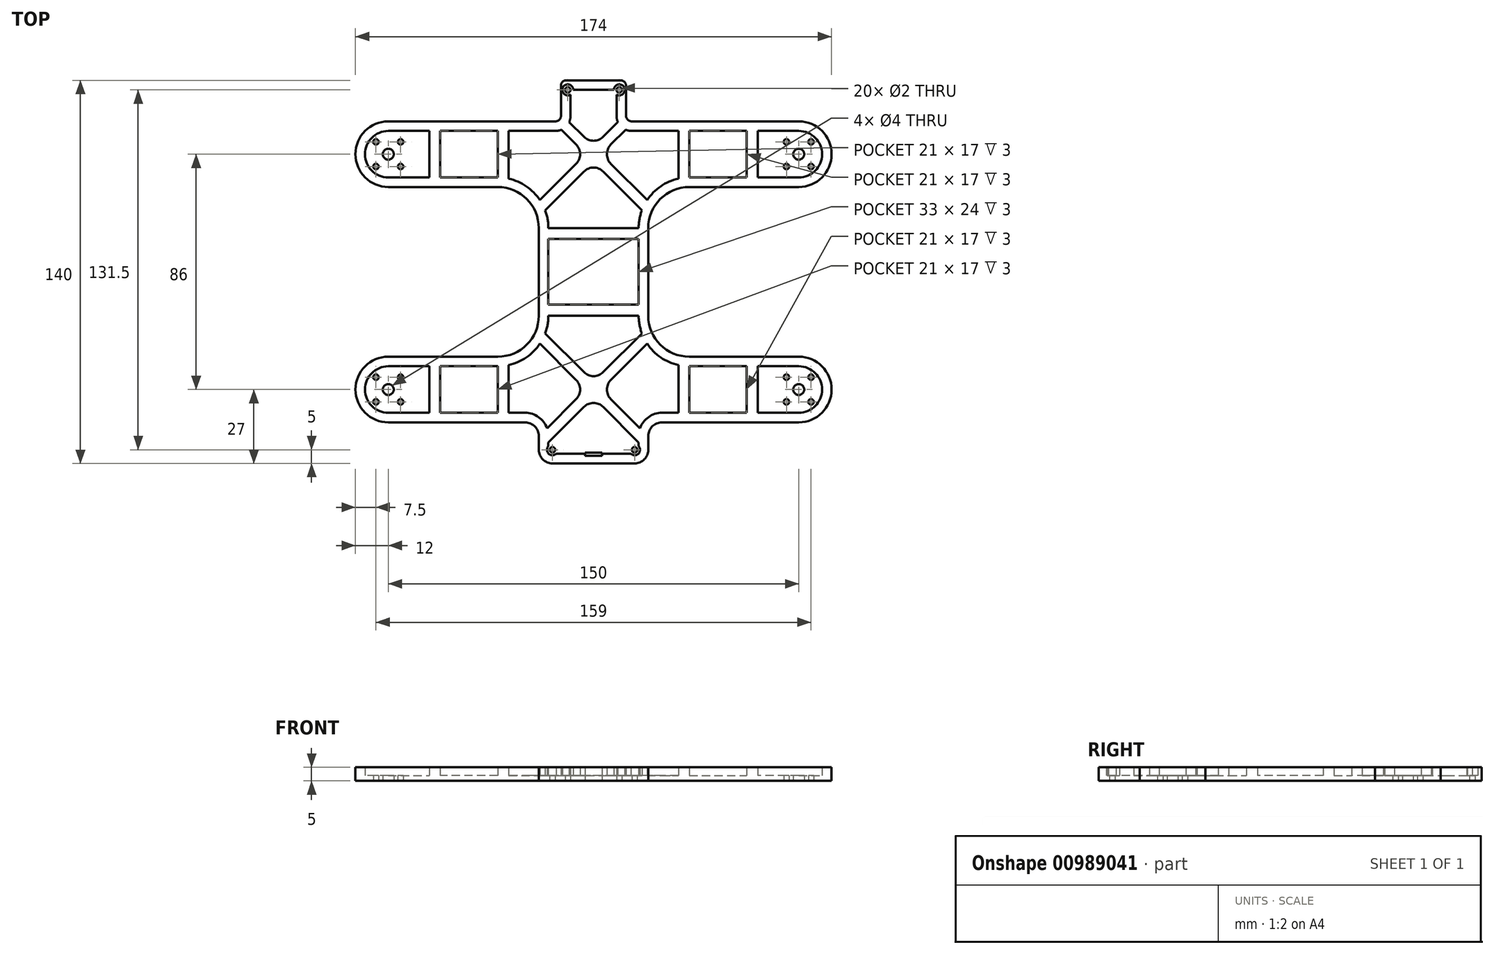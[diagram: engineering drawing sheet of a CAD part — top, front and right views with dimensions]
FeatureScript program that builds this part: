
annotation { "Feature Type Name" : "Feature", "Feature Type Description" : "" }
export const myFeature = defineFeature(function(context is Context, id is Id, definition is map)
    precondition{}
    {
        {
            var Q0;
            Q0=qCreatedBy(makeId("Top.planeOp"),FACE);
            var sketch = newSketch(context, id + "F0", { "sketchPlane" : qUnion([Q0])});
            skLineSegment(sketch, "E0.bottom", {"start": v(-75, 43) * mm, "end": v(75, 43) * mm, "construction": true});
            skLineSegment(sketch, "E0.top", {"start": v(-75, -43) * mm, "end": v(75, -43) * mm, "construction": true});
            skLineSegment(sketch, "E0.left", {"start": v(-75, 43) * mm, "end": v(-75, -43) * mm, "construction": true});
            skLineSegment(sketch, "E0.right", {"start": v(75, 43) * mm, "end": v(75, -43) * mm, "construction": true});
            skPoint(sketch, "E0.middle", {"position": v(0, 0) * mm});
            skLineSegment(sketch, "E1.bottom", {"start": v(-79.5, 47.5) * mm, "end": v(-70.5, 47.5) * mm, "construction": true});
            skLineSegment(sketch, "E1.top", {"start": v(-79.5, 38.5) * mm, "end": v(-70.5, 38.5) * mm, "construction": true});
            skLineSegment(sketch, "E1.left", {"start": v(-79.5, 47.5) * mm, "end": v(-79.5, 38.5) * mm, "construction": true});
            skLineSegment(sketch, "E1.right", {"start": v(-70.5, 47.5) * mm, "end": v(-70.5, 38.5) * mm, "construction": true});
            skPoint(sketch, "E1.middle", {"position": v(-75, 43) * mm});
            skLineSegment(sketch, "E2.MirrorCS", {"start": v(70.5, 47.5) * mm, "end": v(70.5, 38.5) * mm, "construction": true});
            skLineSegment(sketch, "E3.MirrorCS", {"start": v(79.5, 47.5) * mm, "end": v(70.5, 47.5) * mm, "construction": true});
            skLineSegment(sketch, "E4.MirrorCS", {"start": v(79.5, 47.5) * mm, "end": v(79.5, 38.5) * mm, "construction": true});
            skLineSegment(sketch, "E5.MirrorCS", {"start": v(79.5, 38.5) * mm, "end": v(70.5, 38.5) * mm, "construction": true});
            skLineSegment(sketch, "E6.MirrorCS", {"start": v(-70.5, -47.5) * mm, "end": v(-70.5, -38.5) * mm, "construction": true});
            skLineSegment(sketch, "E7.MirrorCS", {"start": v(-79.5, -47.5) * mm, "end": v(-70.5, -47.5) * mm, "construction": true});
            skLineSegment(sketch, "E8.MirrorCS", {"start": v(-79.5, -47.5) * mm, "end": v(-79.5, -38.5) * mm, "construction": true});
            skLineSegment(sketch, "E9.MirrorCS", {"start": v(-79.5, -38.5) * mm, "end": v(-70.5, -38.5) * mm, "construction": true});
            skLineSegment(sketch, "E10.MirrorCS", {"start": v(79.5, -38.5) * mm, "end": v(70.5, -38.5) * mm, "construction": true});
            skLineSegment(sketch, "E11.MirrorCS", {"start": v(70.5, -47.5) * mm, "end": v(70.5, -38.5) * mm, "construction": true});
            skLineSegment(sketch, "E12.MirrorCS", {"start": v(79.5, -47.5) * mm, "end": v(70.5, -47.5) * mm, "construction": true});
            skLineSegment(sketch, "E13.MirrorCS", {"start": v(79.5, -47.5) * mm, "end": v(79.5, -38.5) * mm, "construction": true});
            skLineSegment(sketch, "E14.bottom", {"start": v(-9.9, 70) * mm, "end": v(9.9, 70) * mm});
            skLineSegment(sketch, "E14.top", {"start": v(-15, -70) * mm, "end": v(15, -70) * mm});
            skLineSegment(sketch, "E14.left", {"start": v(-20, 16) * mm, "end": v(-20, -16) * mm});
            skPoint(sketch, "E15.visualSharp", {"position": v(-20, 70) * mm});
            skPoint(sketch, "E16.visualSharp", {"position": v(20, 70) * mm});
            skPoint(sketch, "E17.visualSharp", {"position": v(20, -70) * mm});
            skArc(sketch, "E17.filletArc", {"start": v(15, -70) * mm, "mid": v(18.54, -68.54) * mm, "end": v(20, -65) * mm});
            skPoint(sketch, "E18.visualSharp", {"position": v(-20, -70) * mm});
            skArc(sketch, "E18.filletArc", {"start": v(-20, -65) * mm, "mid": v(-18.54, -68.54) * mm, "end": v(-15, -70) * mm});
            skCircle(sketch, "E19", {"center": v(75, 43) * mm, "radius": 12 * mm});
            skCircle(sketch, "E20.MirrorC", {"center": v(-75, 43) * mm, "radius": 12 * mm});
            skCircle(sketch, "E21.MirrorC", {"center": v(75, -43) * mm, "radius": 12 * mm});
            skCircle(sketch, "E22.MirrorC", {"center": v(-75, -43) * mm, "radius": 12 * mm});
            skLineSegment(sketch, "E23", {"start": v(-75, 55) * mm, "end": v(-13.9, 55) * mm});
            skLineSegment(sketch, "E24.MirrorCS", {"start": v(-75, 31) * mm, "end": v(-35, 31) * mm});
            skPoint(sketch, "E25.newPointB", {"position": v(-20, 31) * mm});
            skArc(sketch, "E25.filletArc", {"start": v(-20, 16) * mm, "mid": v(-24.4, 26.6) * mm, "end": v(-35, 31) * mm});
            skPoint(sketch, "E26.visualSharp", {"position": v(-20, 55) * mm});
            skLineSegment(sketch, "E27.MirrorCS", {"start": v(75, 55) * mm, "end": v(13.9, 55) * mm});
            skArc(sketch, "E28.MirrorCS", {"start": v(20, 16) * mm, "mid": v(24.4, 26.6) * mm, "end": v(35, 31) * mm});
            skLineSegment(sketch, "E29.MirrorCS", {"start": v(75, 31) * mm, "end": v(35, 31) * mm});
            skLineSegment(sketch, "E30.trimOffspring", {"start": v(20, 16) * mm, "end": v(20, -16) * mm});
            skLineSegment(sketch, "E31.MirrorCS", {"start": v(-75, -31) * mm, "end": v(-35, -31) * mm});
            skLineSegment(sketch, "E32.MirrorCS", {"start": v(-75, -55) * mm, "end": v(-25, -55) * mm});
            skArc(sketch, "E33.MirrorCS", {"start": v(-20, -16) * mm, "mid": v(-24.4, -26.6) * mm, "end": v(-35, -31) * mm});
            skArc(sketch, "E34.MirrorCS", {"start": v(20, -16) * mm, "mid": v(24.4, -26.6) * mm, "end": v(35, -31) * mm});
            skLineSegment(sketch, "E35.MirrorCS", {"start": v(75, -31) * mm, "end": v(35, -31) * mm});
            skLineSegment(sketch, "E36.MirrorCS", {"start": v(75, -55) * mm, "end": v(25, -55) * mm});
            skArc(sketch, "E37.MirrorCS", {"start": v(25, -55) * mm, "mid": v(21.46, -56.46) * mm, "end": v(20, -60) * mm});
            skArc(sketch, "E38.MirrorCS", {"start": v(-25, -55) * mm, "mid": v(-21.46, -56.46) * mm, "end": v(-20, -60) * mm});
            skLineSegment(sketch, "E39.trimOffspring", {"start": v(-20, -60) * mm, "end": v(-20, -65) * mm});
            skLineSegment(sketch, "E40.trimOffspring", {"start": v(20, -60) * mm, "end": v(20, -65) * mm});
            skCircle(sketch, "E41", {"center": v(75, 43) * mm, "radius": 2 * mm});
            skCircle(sketch, "E42", {"center": v(79.5, 38.5) * mm, "radius": 1 * mm});
            skCircle(sketch, "E43.MirrorC", {"center": v(70.5, 38.5) * mm, "radius": 1 * mm});
            skCircle(sketch, "E44.MirrorC", {"center": v(70.5, 47.5) * mm, "radius": 1 * mm});
            skCircle(sketch, "E45.MirrorC", {"center": v(79.5, 47.5) * mm, "radius": 1 * mm});
            skCircle(sketch, "E46.MirrorC", {"center": v(-70.5, 38.5) * mm, "radius": 1 * mm});
            skCircle(sketch, "E47.MirrorC", {"center": v(-75, 43) * mm, "radius": 2 * mm});
            skCircle(sketch, "E48.MirrorC", {"center": v(-79.5, 38.5) * mm, "radius": 1 * mm});
            skCircle(sketch, "E49.MirrorC", {"center": v(-79.5, 47.5) * mm, "radius": 1 * mm});
            skCircle(sketch, "E50.MirrorC", {"center": v(-70.5, 47.5) * mm, "radius": 1 * mm});
            skCircle(sketch, "E51.MirrorC", {"center": v(70.5, -38.5) * mm, "radius": 1 * mm});
            skCircle(sketch, "E52.MirrorC", {"center": v(75, -43) * mm, "radius": 2 * mm});
            skCircle(sketch, "E53.MirrorC", {"center": v(79.5, -38.5) * mm, "radius": 1 * mm});
            skCircle(sketch, "E54.MirrorC", {"center": v(79.5, -47.5) * mm, "radius": 1 * mm});
            skCircle(sketch, "E55.MirrorC", {"center": v(70.5, -47.5) * mm, "radius": 1 * mm});
            skCircle(sketch, "E56.MirrorC", {"center": v(-75, -43) * mm, "radius": 2 * mm});
            skCircle(sketch, "E57.MirrorC", {"center": v(-70.5, -38.5) * mm, "radius": 1 * mm});
            skCircle(sketch, "E58.MirrorC", {"center": v(-79.5, -38.5) * mm, "radius": 1 * mm});
            skCircle(sketch, "E59.MirrorC", {"center": v(-79.5, -47.5) * mm, "radius": 1 * mm});
            skCircle(sketch, "E60.MirrorC", {"center": v(-70.5, -47.5) * mm, "radius": 1 * mm});
            skLineSegment(sketch, "E61", {"start": v(0, 43) * mm, "end": v(0, 70) * mm, "construction": true});
            skLineSegment(sketch, "E62", {"start": v(-11.9, 68) * mm, "end": v(-11.9, 57) * mm});
            skLineSegment(sketch, "E63", {"start": v(11.9, 57) * mm, "end": v(11.9, 68) * mm});
            skPoint(sketch, "E64.visualSharp", {"position": v(-11.9, 70) * mm});
            skArc(sketch, "E64.filletArc", {"start": v(-9.9, 70) * mm, "mid": v(-11.31, 69.41) * mm, "end": v(-11.9, 68) * mm});
            skPoint(sketch, "E65.visualSharp", {"position": v(11.9, 70) * mm});
            skArc(sketch, "E65.filletArc", {"start": v(11.9, 68) * mm, "mid": v(11.31, 69.41) * mm, "end": v(9.9, 70) * mm});
            skPoint(sketch, "E66.visualSharp", {"position": v(-11.9, 55) * mm});
            skArc(sketch, "E66.filletArc", {"start": v(-13.9, 55) * mm, "mid": v(-12.49, 55.59) * mm, "end": v(-11.9, 57) * mm});
            skPoint(sketch, "E67.visualSharp", {"position": v(11.9, 55) * mm});
            skArc(sketch, "E67.filletArc", {"start": v(11.9, 57) * mm, "mid": v(12.49, 55.59) * mm, "end": v(13.9, 55) * mm});
            skLineSegment(sketch, "E68", {"start": v(-9.4, 66.5) * mm, "end": v(9.4, 66.5) * mm, "construction": true});
            skCircle(sketch, "E69", {"center": v(-9.4, 66.5) * mm, "radius": 1 * mm});
            skCircle(sketch, "E70.MirrorC", {"center": v(9.4, 66.5) * mm, "radius": 1 * mm});
            skLineSegment(sketch, "E71.bottom", {"start": v(3.1, -67.25) * mm, "end": v(-3.1, -67.25) * mm});
            skLineSegment(sketch, "E71.top", {"start": v(3.1, -66.05) * mm, "end": v(-3.1, -66.05) * mm});
            skLineSegment(sketch, "E71.left", {"start": v(3.1, -67.25) * mm, "end": v(3.1, -66.05) * mm});
            skLineSegment(sketch, "E71.right", {"start": v(-3.1, -67.25) * mm, "end": v(-3.1, -66.05) * mm});
            skPoint(sketch, "E71.middle", {"position": v(0, -66.65) * mm});
            skLineSegment(sketch, "E72", {"start": v(0, -43) * mm, "end": v(0, -66.65) * mm, "construction": true});
            skCircle(sketch, "E73", {"center": v(-15, -65) * mm, "radius": 1 * mm});
            skCircle(sketch, "E74.MirrorC", {"center": v(15, -65) * mm, "radius": 1 * mm});
            skSolve(sketch);
        }
        {
            var Q0;
            Q0 = qSketchRegion(id + "F0", true);
            extrude(context, id + "F1", {"entities" : qUnion([Q0]), "depth" : 2 * mm, "offsetDistance" : 25 * mm});
        }
        {
            var Q0;
            Q0=makeQuery(id+"F1.opExtrude","CAP_FACE",FACE,{"disambiguationData":[OSD([sQuery(id+"F0.wireOp",EDGE,"E14.bottom"),sQuery(id+"F0.wireOp",EDGE,"E14.top"),sQuery(id+"F0.wireOp",EDGE,"E14.left"),sQuery(id+"F0.wireOp",EDGE,"E14.right"),sQuery(id+"F0.wireOp",EDGE,"E15.filletArc"),sQuery(id+"F0.wireOp",EDGE,"E16.filletArc"),sQuery(id+"F0.wireOp",EDGE,"E17.filletArc"),sQuery(id+"F0.wireOp",EDGE,"E18.filletArc"),sQuery(id+"F0.wireOp",EDGE,"E19"),sQuery(id+"F0.wireOp",EDGE,"E20.MirrorC"),sQuery(id+"F0.wireOp",EDGE,"E21.MirrorC"),sQuery(id+"F0.wireOp",EDGE,"E22.MirrorC"),sQuery(id+"F0.wireOp",EDGE,"E23"),sQuery(id+"F0.wireOp",EDGE,"E24.MirrorCS"),sQuery(id+"F0.wireOp",EDGE,"E25.filletArc"),sQuery(id+"F0.wireOp",EDGE,"uSUMrxGN-8YVj-yr1m-6viX-QUxP8JnLmtjf"),sQuery(id+"F0.wireOp",EDGE,"E26.filletArc"),sQuery(id+"F0.wireOp",EDGE,"6cd38d5e-6e8f-4e99-a3e8-9a7adae25e910.MirrorCS"),sQuery(id+"F0.wireOp",EDGE,"E27.MirrorCS"),sQuery(id+"F0.wireOp",EDGE,"E28.MirrorCS"),sQuery(id+"F0.wireOp",EDGE,"E29.MirrorCS"),sQuery(id+"F0.wireOp",EDGE,"E30.trimOffspring"),sQuery(id+"F0.wireOp",EDGE,"E31.MirrorCS"),sQuery(id+"F0.wireOp",EDGE,"E32.MirrorCS"),sQuery(id+"F0.wireOp",EDGE,"E33.MirrorCS"),sQuery(id+"F0.wireOp",EDGE,"E34.MirrorCS"),sQuery(id+"F0.wireOp",EDGE,"E35.MirrorCS"),sQuery(id+"F0.wireOp",EDGE,"E36.MirrorCS"),sQuery(id+"F0.wireOp",EDGE,"E37.MirrorCS"),sQuery(id+"F0.wireOp",EDGE,"E38.MirrorCS"),sQuery(id+"F0.wireOp",EDGE,"E39.trimOffspring"),sQuery(id+"F0.wireOp",EDGE,"E40.trimOffspring")])],"isStart":false});
            var sketch = newSketch(context, id + "F2", { "sketchPlane" : qUnion([Q0])});
            skArc(sketch, "E75.0.0", {"start": v(75, 31) * mm, "mid": v(87, 43) * mm, "end": v(75, 55) * mm});
            skLineSegment(sketch, "E75.0.1", {"start": v(75, 55) * mm, "end": v(75, 55) * mm});
            skLineSegment(sketch, "E75.0.9", {"start": v(-25, 55) * mm, "end": v(-75, 55) * mm});
            skArc(sketch, "E75.0.10", {"start": v(-75, 55) * mm, "mid": v(-87, 43) * mm, "end": v(-75, 31) * mm});
            skLineSegment(sketch, "E75.0.11", {"start": v(-75, 31) * mm, "end": v(-35, 31) * mm});
            skArc(sketch, "E75.0.12", {"start": v(-35, 31) * mm, "mid": v(-24.4, 26.6) * mm, "end": v(-20, 16) * mm});
            skLineSegment(sketch, "E75.0.13", {"start": v(-20, 16) * mm, "end": v(-20, -16) * mm});
            skArc(sketch, "E75.0.14", {"start": v(-20, -16) * mm, "mid": v(-24.4, -26.6) * mm, "end": v(-35, -31) * mm});
            skLineSegment(sketch, "E75.0.15", {"start": v(-35, -31) * mm, "end": v(-75, -31) * mm});
            skArc(sketch, "E75.0.16", {"start": v(-75, -31) * mm, "mid": v(-87, -43) * mm, "end": v(-75, -55) * mm});
            skLineSegment(sketch, "E75.0.17", {"start": v(-75, -55) * mm, "end": v(-25, -55) * mm});
            skArc(sketch, "E75.0.18", {"start": v(-25, -55) * mm, "mid": v(-21.46, -56.46) * mm, "end": v(-20, -60) * mm});
            skLineSegment(sketch, "E75.0.19", {"start": v(-20, -60) * mm, "end": v(-20, -65) * mm});
            skArc(sketch, "E75.0.20", {"start": v(-20, -65) * mm, "mid": v(-18.54, -68.54) * mm, "end": v(-15, -70) * mm});
            skLineSegment(sketch, "E75.0.21", {"start": v(-15, -70) * mm, "end": v(15, -70) * mm});
            skArc(sketch, "E75.0.22", {"start": v(15, -70) * mm, "mid": v(18.54, -68.54) * mm, "end": v(20, -65) * mm});
            skLineSegment(sketch, "E75.0.23", {"start": v(20, -65) * mm, "end": v(20, -60) * mm});
            skArc(sketch, "E75.0.24", {"start": v(20, -60) * mm, "mid": v(21.46, -56.46) * mm, "end": v(25, -55) * mm});
            skLineSegment(sketch, "E75.0.25", {"start": v(25, -55) * mm, "end": v(75, -55) * mm});
            skArc(sketch, "E75.0.26", {"start": v(75, -55) * mm, "mid": v(87, -43) * mm, "end": v(75, -31) * mm});
            skLineSegment(sketch, "E75.0.27", {"start": v(75, -31) * mm, "end": v(35, -31) * mm});
            skArc(sketch, "E75.0.28", {"start": v(35, -31) * mm, "mid": v(24.4, -26.6) * mm, "end": v(20, -16) * mm});
            skLineSegment(sketch, "E75.0.29", {"start": v(20, -16) * mm, "end": v(20, 16) * mm});
            skArc(sketch, "E75.0.30", {"start": v(20, 16) * mm, "mid": v(24.4, 26.6) * mm, "end": v(35, 31) * mm});
            skLineSegment(sketch, "E75.0.31", {"start": v(35, 31) * mm, "end": v(75, 31) * mm});
            skLineSegment(sketch, "E76.5", {"start": v(-16.5, -62.33) * mm, "end": v(-16.5, -63.68) * mm});
            skArc(sketch, "E76.6", {"start": v(-25, -51.5) * mm, "mid": v(-20.1, -53.06) * mm, "end": v(-16.99, -57.16) * mm});
            skLineSegment(sketch, "E76.7", {"start": v(-75, -51.5) * mm, "end": v(-60, -51.5) * mm});
            skArc(sketch, "E76.8", {"start": v(-75, -34.5) * mm, "mid": v(-83.5, -43) * mm, "end": v(-75, -51.5) * mm});
            skLineSegment(sketch, "E76.9", {"start": v(-35, -34.5) * mm, "end": v(-56, -34.5) * mm});
            skArc(sketch, "E76.10", {"start": v(-16.5, -16) * mm, "mid": v(-16.8, -19.3) * mm, "end": v(-17.68, -22.5) * mm});
            skArc(sketch, "E76.11", {"start": v(-75, 51.5) * mm, "mid": v(-83.5, 43) * mm, "end": v(-75, 34.5) * mm});
            skLineSegment(sketch, "E76.12", {"start": v(-75, 34.5) * mm, "end": v(-60, 34.5) * mm});
            skArc(sketch, "E76.13", {"start": v(-31, 34.06) * mm, "mid": v(-20.57, 27.58) * mm, "end": v(-16.5, 16) * mm});
            skLineSegment(sketch, "E76.14", {"start": v(-16.5, 12) * mm, "end": v(-16.5, -12) * mm});
            skArc(sketch, "E76.17", {"start": v(16.99, -57.16) * mm, "mid": v(20.1, -53.06) * mm, "end": v(25, -51.5) * mm});
            skLineSegment(sketch, "E76.18", {"start": v(25, -51.5) * mm, "end": v(31, -51.5) * mm});
            skArc(sketch, "E76.19", {"start": v(75, -51.5) * mm, "mid": v(83.5, -43) * mm, "end": v(75, -34.5) * mm});
            skLineSegment(sketch, "E76.20", {"start": v(-25, 51.5) * mm, "end": v(-31, 51.5) * mm});
            skLineSegment(sketch, "E76.21", {"start": v(75, -34.5) * mm, "end": v(60, -34.5) * mm});
            skArc(sketch, "E76.22", {"start": v(31, -34.06) * mm, "mid": v(24.54, -31.26) * mm, "end": v(19.6, -26.24) * mm});
            skLineSegment(sketch, "E76.23", {"start": v(16.5, -12) * mm, "end": v(16.5, 12) * mm});
            skArc(sketch, "E76.24", {"start": v(16.5, 16) * mm, "mid": v(16.8, 19.3) * mm, "end": v(17.68, 22.5) * mm});
            skLineSegment(sketch, "E76.25", {"start": v(35, 34.5) * mm, "end": v(56, 34.5) * mm});
            skArc(sketch, "E76.26", {"start": v(75, 34.5) * mm, "mid": v(83.5, 43) * mm, "end": v(75, 51.5) * mm});
            skLineSegment(sketch, "E76.27", {"start": v(75, 51.5) * mm, "end": v(60, 51.5) * mm});
            skLineSegment(sketch, "E77", {"start": v(-16.5, -16) * mm, "end": v(16.5, -16) * mm});
            skLineSegment(sketch, "E78", {"start": v(-16.5, -12) * mm, "end": v(16.5, -12) * mm});
            skLineSegment(sketch, "E79.MirrorCS", {"start": v(-16.5, 12) * mm, "end": v(16.5, 12) * mm});
            skLineSegment(sketch, "E80.MirrorCS", {"start": v(-16.5, 16) * mm, "end": v(16.5, 16) * mm});
            skLineSegment(sketch, "E81", {"start": v(60, -51.5) * mm, "end": v(60, -34.5) * mm});
            skLineSegment(sketch, "E82", {"start": v(56, -51.5) * mm, "end": v(56, -34.5) * mm});
            skLineSegment(sketch, "E83.trimOffspring", {"start": v(60, -51.5) * mm, "end": v(75, -51.5) * mm});
            skLineSegment(sketch, "E84.trimOffspring", {"start": v(56, -34.5) * mm, "end": v(35, -34.5) * mm});
            skLineSegment(sketch, "E85.MirrorCS", {"start": v(-56, -51.5) * mm, "end": v(-56, -34.5) * mm});
            skLineSegment(sketch, "E86.MirrorCS", {"start": v(-60, -51.5) * mm, "end": v(-60, -34.5) * mm});
            skLineSegment(sketch, "E87.MirrorCS", {"start": v(60, 51.5) * mm, "end": v(60, 34.5) * mm});
            skLineSegment(sketch, "E88.MirrorCS", {"start": v(56, 51.5) * mm, "end": v(56, 34.5) * mm});
            skLineSegment(sketch, "E89.MirrorCS", {"start": v(-56, 51.5) * mm, "end": v(-56, 34.5) * mm});
            skLineSegment(sketch, "E90.MirrorCS", {"start": v(-60, 51.5) * mm, "end": v(-60, 34.5) * mm});
            skLineSegment(sketch, "E91", {"start": v(16.99, -57.16) * mm, "end": v(6.36, -46.54) * mm});
            skLineSegment(sketch, "E92", {"start": v(-19.6, -26.24) * mm, "end": v(-6.36, -39.46) * mm});
            skLineSegment(sketch, "E93", {"start": v(75, -43) * mm, "end": v(-75, -43) * mm, "construction": true});
            skLineSegment(sketch, "E94", {"start": v(0, -43) * mm, "end": v(7.2, -50.2) * mm, "construction": true});
            skArc(sketch, "E95.trimOffspring", {"start": v(-19.6, -26.24) * mm, "mid": v(-24.54, -31.26) * mm, "end": v(-31, -34.06) * mm});
            skLineSegment(sketch, "E96.MirrorCS", {"start": v(19.6, -26.24) * mm, "end": v(6.36, -39.46) * mm});
            skLineSegment(sketch, "E97.MirrorCS", {"start": v(-16.99, -57.16) * mm, "end": v(-6.36, -46.54) * mm});
            skLineSegment(sketch, "E98.trimOffspring", {"start": v(-3.54, -36.64) * mm, "end": v(-17.68, -22.5) * mm});
            skLineSegment(sketch, "E99.trimOffspring", {"start": v(-3.54, -49.36) * mm, "end": v(-16.5, -62.33) * mm});
            skLineSegment(sketch, "E100.trimOffspring", {"start": v(3.54, -36.64) * mm, "end": v(17.68, -22.5) * mm});
            skLineSegment(sketch, "E101.trimOffspring", {"start": v(3.54, -49.36) * mm, "end": v(16.5, -62.33) * mm});
            skPoint(sketch, "E102.visualSharp", {"position": v(2.83, -43) * mm});
            skArc(sketch, "E102.filletArc", {"start": v(6.36, -39.46) * mm, "mid": v(4.9, -43) * mm, "end": v(6.36, -46.54) * mm});
            skPoint(sketch, "E103.visualSharp", {"position": v(0, -45.83) * mm});
            skArc(sketch, "E103.filletArc", {"start": v(3.54, -49.36) * mm, "mid": v(0, -47.9) * mm, "end": v(-3.54, -49.36) * mm});
            skPoint(sketch, "E104.visualSharp", {"position": v(-2.83, -43) * mm});
            skArc(sketch, "E104.filletArc", {"start": v(-6.36, -46.54) * mm, "mid": v(-4.9, -43) * mm, "end": v(-6.36, -39.46) * mm});
            skPoint(sketch, "E105.visualSharp", {"position": v(0, -40.17) * mm});
            skArc(sketch, "E105.filletArc", {"start": v(-3.54, -36.64) * mm, "mid": v(0, -38.1) * mm, "end": v(3.54, -36.64) * mm});
            skArc(sketch, "E106.trimOffspring", {"start": v(17.68, -22.5) * mm, "mid": v(16.8, -19.3) * mm, "end": v(16.5, -16) * mm});
            skLineSegment(sketch, "E107.MirrorCS", {"start": v(3.54, 36.64) * mm, "end": v(17.68, 22.5) * mm});
            skPoint(sketch, "E108.MirrorP", {"position": v(0, 40.17) * mm});
            skArc(sketch, "E109.MirrorCS", {"start": v(-3.54, 36.64) * mm, "mid": v(0, 38.1) * mm, "end": v(3.54, 36.64) * mm});
            skLineSegment(sketch, "E110.MirrorCS", {"start": v(-3.54, 36.64) * mm, "end": v(-17.68, 22.5) * mm});
            skLineSegment(sketch, "E111.MirrorCS", {"start": v(-19.6, 26.24) * mm, "end": v(-6.36, 39.46) * mm});
            skLineSegment(sketch, "E112.MirrorCS", {"start": v(-3.54, 49.36) * mm, "end": v(-8.9, 54.72) * mm});
            skLineSegment(sketch, "E113.MirrorCS", {"start": v(3.54, 49.36) * mm, "end": v(8.9, 54.72) * mm});
            skLineSegment(sketch, "E114.MirrorCS", {"start": v(11.76, 51.93) * mm, "end": v(6.36, 46.54) * mm});
            skArc(sketch, "E115.MirrorCS", {"start": v(6.36, 39.46) * mm, "mid": v(4.9, 43) * mm, "end": v(6.36, 46.54) * mm});
            skArc(sketch, "E116.MirrorCS", {"start": v(3.54, 49.36) * mm, "mid": v(0, 47.9) * mm, "end": v(-3.54, 49.36) * mm});
            skArc(sketch, "E117.MirrorCS", {"start": v(-6.36, 46.54) * mm, "mid": v(-4.9, 43) * mm, "end": v(-6.36, 39.46) * mm});
            skLineSegment(sketch, "E118.MirrorCS", {"start": v(19.6, 26.24) * mm, "end": v(6.36, 39.46) * mm});
            skLineSegment(sketch, "E119.trimOffspring", {"start": v(60, 34.5) * mm, "end": v(75, 34.5) * mm});
            skArc(sketch, "E120.trimOffspring", {"start": v(19.6, 26.24) * mm, "mid": v(24.54, 31.26) * mm, "end": v(31, 34.06) * mm});
            skLineSegment(sketch, "E121.trimOffspring", {"start": v(-60, 51.5) * mm, "end": v(-75, 51.5) * mm});
            skLineSegment(sketch, "E122.trimOffspring", {"start": v(-56, 34.5) * mm, "end": v(-35, 34.5) * mm});
            skLineSegment(sketch, "E123.trimOffspring", {"start": v(56, 51.5) * mm, "end": v(35, 51.5) * mm});
            skLineSegment(sketch, "E124.trimOffspring", {"start": v(-56, -51.5) * mm, "end": v(-35, -51.5) * mm});
            skLineSegment(sketch, "E125.trimOffspring", {"start": v(-60, -34.5) * mm, "end": v(-75, -34.5) * mm});
            skLineSegment(sketch, "E126", {"start": v(35, -34.5) * mm, "end": v(35, -51.5) * mm});
            skLineSegment(sketch, "E127", {"start": v(31, -51.5) * mm, "end": v(31, -34.06) * mm});
            skLineSegment(sketch, "E128.trimOffspring", {"start": v(35, -51.5) * mm, "end": v(56, -51.5) * mm});
            skLineSegment(sketch, "E129.MirrorCS", {"start": v(-31, -51.5) * mm, "end": v(-31, -34.06) * mm});
            skLineSegment(sketch, "E130.MirrorCS", {"start": v(-35, -34.5) * mm, "end": v(-35, -51.5) * mm});
            skLineSegment(sketch, "E131.trimOffspring", {"start": v(-31, -51.5) * mm, "end": v(-25, -51.5) * mm});
            skLineSegment(sketch, "E132.MirrorCS", {"start": v(31, 51.5) * mm, "end": v(31, 34.06) * mm});
            skLineSegment(sketch, "E133.MirrorCS", {"start": v(35, 34.5) * mm, "end": v(35, 51.5) * mm});
            skLineSegment(sketch, "E134.MirrorCS", {"start": v(-31, 51.5) * mm, "end": v(-31, 34.06) * mm});
            skLineSegment(sketch, "E135.MirrorCS", {"start": v(-35, 34.5) * mm, "end": v(-35, 51.5) * mm});
            skLineSegment(sketch, "E136.trimOffspring", {"start": v(-35, 51.5) * mm, "end": v(-56, 51.5) * mm});
            skLineSegment(sketch, "E137.trimOffspring", {"start": v(78.4, 51.5) * mm, "end": v(31, 51.5) * mm});
            skLineSegment(sketch, "E138.0", {"start": v(-75, 55) * mm, "end": v(-13.9, 55) * mm});
            skPoint(sketch, "E139.0", {"position": v(-11.9, 62.5) * mm});
            skLineSegment(sketch, "E140.0", {"start": v(-11.9, 68) * mm, "end": v(-11.9, 57) * mm});
            skPoint(sketch, "E141.0", {"position": v(-11.31, 69.41) * mm});
            skArc(sketch, "E142.0", {"start": v(11.9, 57) * mm, "mid": v(12.49, 55.59) * mm, "end": v(13.9, 55) * mm});
            skPoint(sketch, "E143.0", {"position": v(-11.9, 57) * mm});
            skPoint(sketch, "E144.0", {"position": v(-12.49, 55.59) * mm});
            skArc(sketch, "E145.0", {"start": v(-13.9, 55) * mm, "mid": v(-12.49, 55.59) * mm, "end": v(-11.9, 57) * mm});
            skLineSegment(sketch, "E146.0", {"start": v(75, 55) * mm, "end": v(13.9, 55) * mm});
            skPoint(sketch, "E147.0", {"position": v(11.9, 62.5) * mm});
            skArc(sketch, "E148.0", {"start": v(11.9, 68) * mm, "mid": v(11.31, 69.41) * mm, "end": v(9.9, 70) * mm});
            skLineSegment(sketch, "E149.0", {"start": v(11.9, 57) * mm, "end": v(11.9, 68) * mm});
            skArc(sketch, "E150.0.2", {"start": v(13.9, 55) * mm, "mid": v(12.49, 55.59) * mm, "end": v(11.9, 57) * mm});
            skLineSegment(sketch, "E150.0.5", {"start": v(9.9, 70) * mm, "end": v(-9.9, 70) * mm});
            skArc(sketch, "E150.0.6", {"start": v(-9.9, 70) * mm, "mid": v(-11.31, 69.41) * mm, "end": v(-11.9, 68) * mm});
            skArc(sketch, "E150.0.8", {"start": v(-11.9, 57) * mm, "mid": v(-12.49, 55.59) * mm, "end": v(-13.9, 55) * mm});
            skLineSegment(sketch, "E150.0.9", {"start": v(-13.9, 55) * mm, "end": v(-75, 55) * mm});
            skLineSegment(sketch, "E151.0", {"start": v(75, 51.5) * mm, "end": v(13.9, 51.5) * mm});
            skArc(sketch, "E151.1", {"start": v(13.9, 51.5) * mm, "mid": v(10.01, 53.11) * mm, "end": v(8.4, 57) * mm});
            skLineSegment(sketch, "E151.2", {"start": v(8.4, 57) * mm, "end": v(8.4, 64.77) * mm});
            skLineSegment(sketch, "E151.3", {"start": v(-75, 51.5) * mm, "end": v(-13.9, 51.5) * mm});
            skArc(sketch, "E151.4", {"start": v(-8.4, 57) * mm, "mid": v(-10.01, 53.11) * mm, "end": v(-13.9, 51.5) * mm});
            skLineSegment(sketch, "E151.5", {"start": v(-8.4, 64.77) * mm, "end": v(-8.4, 57) * mm});
            skLineSegment(sketch, "E151.6", {"start": v(7.4, 66.5) * mm, "end": v(-7.4, 66.5) * mm});
            skCircle(sketch, "E152.0", {"center": v(-9.4, 66.5) * mm, "radius": 1 * mm});
            skCircle(sketch, "E153.0", {"center": v(9.4, 66.5) * mm, "radius": 1 * mm});
            skCircle(sketch, "E154", {"center": v(-9.4, 66.5) * mm, "radius": 2 * mm});
            skCircle(sketch, "E155.MirrorC", {"center": v(9.4, 66.5) * mm, "radius": 2 * mm});
            skLineSegment(sketch, "E156.trimOffspring", {"start": v(-11.76, 51.93) * mm, "end": v(-6.36, 46.54) * mm});
            skPoint(sketch, "E157.MirrorCS.start.orphan", {"position": v(-16.99, 57.16) * mm});
            skPoint(sketch, "E158.trimOffspring.end.orphan", {"position": v(-16.5, 62.33) * mm});
            skPoint(sketch, "E159.orphan", {"position": v(16.5, 62.33) * mm});
            skPoint(sketch, "E160.orphan", {"position": v(16.99, 57.16) * mm});
            skCircle(sketch, "E161", {"center": v(-15, -65) * mm, "radius": 2 * mm});
            skCircle(sketch, "E162.MirrorC", {"center": v(15, -65) * mm, "radius": 2 * mm});
            skLineSegment(sketch, "E163.trimOffspring", {"start": v(-13.68, -66.5) * mm, "end": v(-3.1, -66.5) * mm});
            skLineSegment(sketch, "E164.trimOffspring", {"start": v(16.5, -63.68) * mm, "end": v(16.5, -62.33) * mm});
            skPoint(sketch, "E165.0", {"position": v(-3.1, -66.65) * mm});
            skLineSegment(sketch, "E166.0", {"start": v(-3.1, -67.25) * mm, "end": v(-3.1, -66.05) * mm});
            skLineSegment(sketch, "E167.0", {"start": v(3.1, -67.25) * mm, "end": v(-3.1, -67.25) * mm});
            skLineSegment(sketch, "E168.0", {"start": v(3.1, -67.25) * mm, "end": v(3.1, -66.05) * mm});
            skLineSegment(sketch, "E169.trimOffspring", {"start": v(3.1, -66.5) * mm, "end": v(13.68, -66.5) * mm});
            skSolve(sketch);
        }
        {
            var Q0;
            Q0 = qSketchRegion(id + "F2", true);
            extrude(context, id + "F3", {"entities" : qUnion([Q0]), "operationType" : NewBodyOperationType.ADD, "depth" : 3 * mm, "offsetDistance" : 25 * mm});
        }
    });
